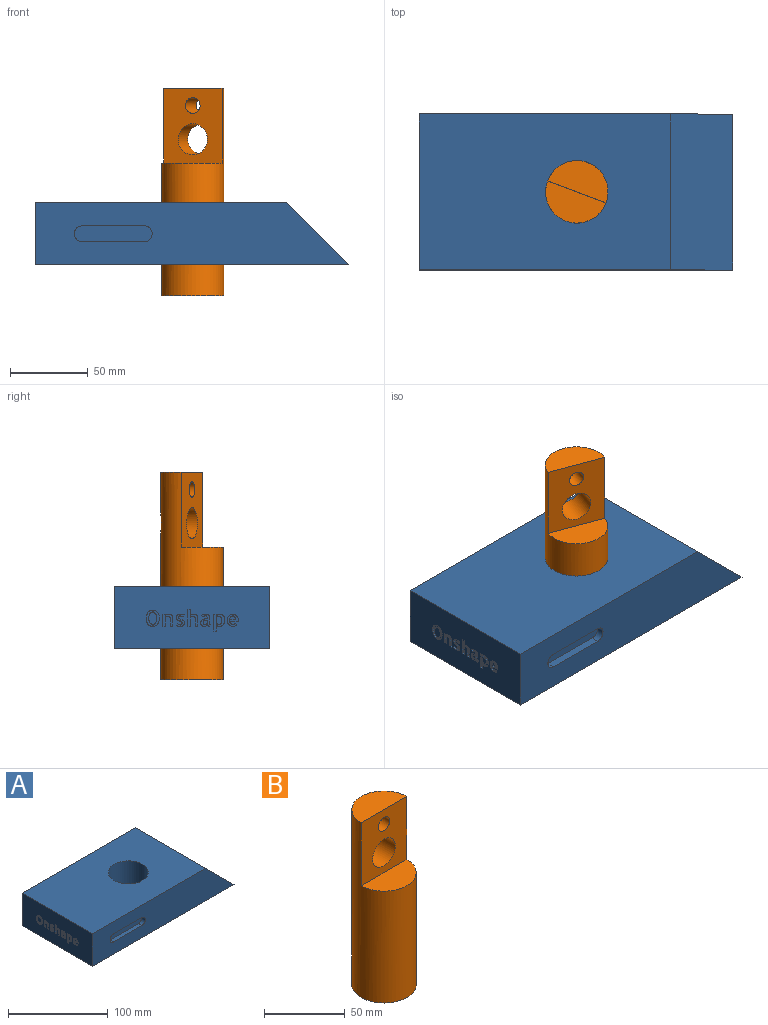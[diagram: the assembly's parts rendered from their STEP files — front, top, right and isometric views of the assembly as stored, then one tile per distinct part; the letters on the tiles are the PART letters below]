
ASSEMBLY  parts=2 mates=1
PART A: 284 faces, bbox 201x100x40 mm
  f0: plane 201x40mm, normal (0,1,0), area 7240mm2, adj f3,f4,f5,f252
  f1: plane 201x40mm, normal (0,-1,0), area 6761.5mm2, adj f3,f4,f5,f252,f269,f270,f271,f272
  f2: cylinder r=20mm len=40mm, axis (0,0,-1), area 5026.5mm2, adj f4,f5
  f3: plane 100x40mm, normal (0.71,0,0.71), area 5656.9mm2, adj f0,f1,f4,f5
  f4: plane 161x100mm, normal (0,0,1), area 14843.4mm2, adj f0,f1,f2,f3,f252
  f5: plane 201x100mm, normal (0,0,-1), area 17037mm2, adj f0,f1,f2,f3,f252,f274,f275,f276
  f6: extruded ~2.17x1mm, area 2.2mm2, adj f7,f251,f252,f253
  f7: extruded ~2.16x1mm, area 2.2mm2, adj f6,f8,f252,f253
  f8: extruded ~1.59x1mm, area 1.8mm2, adj f7,f9,f252,f253
  f9: extruded ~1.25x1mm, area 1.6mm2, adj f8,f10,f252,f253
  f10: extruded ~1.57x1mm, area 1.6mm2, adj f9,f11,f252,f253
  f11: plane 1.37x1mm, normal (0,1,0), area 1.4mm2, adj f10,f12,f252,f253
  f12: extruded ~1x0.88mm, area 0.9mm2, adj f11,f13,f252,f253
  f13: extruded ~1x0.71mm, area 1mm2, adj f12,f14,f252,f253
  f14: extruded ~1.15x1mm, area 1.3mm2, adj f13,f15,f252,f253
  f15: extruded ~1.66x1mm, area 1.7mm2, adj f14,f16,f252,f253
  f16: extruded ~1.67x1mm, area 1.7mm2, adj f15,f17,f252,f253
  f17: extruded ~1.16x1mm, area 1.3mm2, adj f16,f18,f252,f253
  f18: extruded ~1x0.72mm, area 1mm2, adj f17,f19,f252,f253
  f19: extruded ~1x0.86mm, area 0.9mm2, adj f18,f20,f252,f253
  f20: plane 1.36x1mm, normal (0,1,0), area 1.4mm2, adj f19,f21,f252,f253
  f21: extruded ~1.57x1mm, area 1.6mm2, adj f20,f22,f252,f253
  f22: extruded ~1.26x1mm, area 1.6mm2, adj f21,f251,f252,f253
  f23: plane 1.36x1mm, normal (0,-1,0), area 1.4mm2, adj f24,f236,f252,f268
  f24: extruded ~1.56x1mm, area 1.6mm2, adj f23,f25,f252,f268
  f25: extruded ~1.25x1.01mm, area 1.6mm2, adj f24,f26,f252,f268
  f26: extruded ~1.59x1mm, area 1.8mm2, adj f25,f27,f252,f268
  f27: extruded ~2.16x1mm, area 2.2mm2, adj f26,f28,f252,f268
  f28: extruded ~2.17x1mm, area 2.2mm2, adj f27,f29,f252,f268
  f29: extruded ~1.6x1mm, area 1.8mm2, adj f28,f30,f252,f268
  f30: extruded ~1.24x1mm, area 1.6mm2, adj f29,f31,f252,f268
  f31: extruded ~1.57x1mm, area 1.6mm2, adj f30,f32,f252,f268
  f32: plane 1.36x1mm, normal (0,-1,0), area 1.4mm2, adj f31,f33,f252,f268
  f33: extruded ~1x0.88mm, area 0.9mm2, adj f32,f34,f252,f268
  f34: extruded ~1x0.71mm, area 1mm2, adj f33,f35,f252,f268
  f35: extruded ~1.15x1mm, area 1.3mm2, adj f34,f36,f252,f268
  f36: extruded ~1.67x1mm, area 1.7mm2, adj f35,f37,f252,f268
  f37: extruded ~1.67x1mm, area 1.7mm2, adj f36,f38,f252,f268
  f38: extruded ~1.15x1mm, area 1.3mm2, adj f37,f39,f252,f268
  f39: extruded ~1x0.72mm, area 1mm2, adj f38,f236,f252,f268
  f40: plane 1.48x1mm, normal (0,0,-1), area 1.5mm2, adj f41,f237,f252,f267
  f41: plane 1x0.78mm, normal (0,0.98,-0.22), area 0.8mm2, adj f40,f42,f252,f267
  f42: plane 6.96x1mm, normal (0,1,0), area 7mm2, adj f41,f43,f252,f267
  f43: plane 1.66x1mm, normal (0,0,1), area 1.7mm2, adj f42,f237,f252,f267
  f44: extruded ~1x0.85mm, area 1.1mm2, adj f45,f238,f252,f266
  f45: extruded ~1x0.54mm, area 0.7mm2, adj f44,f46,f252,f266
  f46: extruded ~1x0.64mm, area 0.7mm2, adj f45,f47,f252,f266
  f47: extruded ~1x0.68mm, area 0.7mm2, adj f46,f48,f252,f266
  f48: extruded ~1x0.67mm, area 0.7mm2, adj f47,f49,f252,f266
  f49: plane 4.35x1mm, normal (0,1,0), area 4.4mm2, adj f48,f50,f252,f266
  f50: plane 1.67x1mm, normal (0,0,1), area 1.7mm2, adj f49,f51,f252,f266
  f51: plane 4.21x1mm, normal (0,-1,0), area 4.2mm2, adj f50,f52,f252,f266
  f52: extruded ~1x0.89mm, area 0.9mm2, adj f51,f53,f252,f266
  f53: extruded ~1x0.76mm, area 0.8mm2, adj f52,f54,f252,f266
  f54: extruded ~1x0.52mm, area 0.7mm2, adj f53,f55,f252,f266
  f55: extruded ~1x0.73mm, area 0.8mm2, adj f54,f56,f252,f266
  f56: extruded ~1x0.52mm, area 0.5mm2, adj f55,f57,f252,f266
  f57: extruded ~1x0.63mm, area 0.7mm2, adj f56,f58,f252,f266
  f58: plane 1.06x1mm, normal (0,-1,0), area 1.1mm2, adj f57,f59,f252,f266
  f59: extruded ~1x0.8mm, area 0.9mm2, adj f58,f60,f252,f266
  f60: extruded ~1x0.84mm, area 0.9mm2, adj f59,f238,f252,f266
  f61: extruded ~1.13x1mm, area 1.2mm2, adj f62,f239,f252,f265
  f62: extruded ~1x0.94mm, area 1mm2, adj f61,f63,f252,f265
  f63: extruded ~1x0.71mm, area 0.9mm2, adj f62,f64,f252,f265
  f64: extruded ~1x0.78mm, area 0.9mm2, adj f63,f65,f252,f265
  f65: extruded ~1x0.9mm, area 0.9mm2, adj f64,f66,f252,f265
  f66: plane 1.37x1mm, normal (0,1,0), area 1.4mm2, adj f65,f67,f252,f265
  f67: extruded ~1x0.56mm, area 0.6mm2, adj f66,f68,f252,f265
  f68: extruded ~1x0.62mm, area 0.7mm2, adj f67,f69,f252,f265
  f69: extruded ~1x0.53mm, area 0.6mm2, adj f68,f70,f252,f265
  f70: extruded ~1x0.54mm, area 0.6mm2, adj f69,f71,f252,f265
  f71: plane 1.47x1mm, normal (0,1,0), area 1.5mm2, adj f70,f72,f252,f265
  f72: extruded ~1x0.47mm, area 0.5mm2, adj f71,f73,f252,f265
  f73: extruded ~1x0.47mm, area 0.5mm2, adj f72,f239,f252,f265
  f74: plane 1.14x1mm, normal (0,0.9,0.43), area 1.3mm2, adj f75,f240,f252,f264
  f75: extruded ~1x0.79mm, area 0.8mm2, adj f74,f76,f252,f264
  f76: extruded ~1x0.83mm, area 0.8mm2, adj f75,f77,f252,f264
  f77: plane 1.36x1mm, normal (0,-1,0), area 1.4mm2, adj f76,f78,f252,f264
  f78: extruded ~1.14x1mm, area 1.2mm2, adj f77,f240,f252,f264
  f79: plane 1.11x1mm, normal (0,-0.85,-0.53), area 1.3mm2, adj f80,f241,f252,f263
  f80: extruded ~1x0.65mm, area 0.7mm2, adj f79,f81,f252,f263
  f81: extruded ~1x0.95mm, area 1mm2, adj f80,f82,f252,f263
  f82: plane 1x0.07mm, normal (0,0,-1), area 0.1mm2, adj f81,f83,f252,f263
  f83: plane 1.28x1mm, normal (0,1,0), area 1.3mm2, adj f82,f84,f252,f263
  f84: extruded ~1x0.63mm, area 0.6mm2, adj f83,f85,f252,f263
  f85: extruded ~1x0.57mm, area 0.6mm2, adj f84,f86,f252,f263
  f86: extruded ~1x0.57mm, area 0.6mm2, adj f85,f241,f252,f263
  f87: plane 1.46x1mm, normal (0,-1,0), area 1.5mm2, adj f88,f242,f252,f262
  f88: extruded ~1x0.84mm, area 0.9mm2, adj f87,f89,f252,f262
  f89: extruded ~1x0.78mm, area 0.9mm2, adj f88,f90,f252,f262
  f90: extruded ~1x0.61mm, area 0.8mm2, adj f89,f91,f252,f262
  f91: extruded ~1x0.91mm, area 1mm2, adj f90,f92,f252,f262
  f92: extruded ~1x0.93mm, area 1mm2, adj f91,f93,f252,f262
  f93: extruded ~1x0.69mm, area 0.9mm2, adj f92,f94,f252,f262
  f94: extruded ~1x0.76mm, area 0.9mm2, adj f93,f95,f252,f262
  f95: extruded ~1x0.95mm, area 1mm2, adj f94,f96,f252,f262
  f96: plane 1.3x1mm, normal (0,-1,0), area 1.3mm2, adj f95,f97,f252,f262
  f97: extruded ~1x0.72mm, area 0.8mm2, adj f96,f98,f252,f262
  f98: extruded ~1x0.57mm, area 0.6mm2, adj f97,f99,f252,f262
  f99: extruded ~1x0.56mm, area 0.6mm2, adj f98,f242,f252,f262
  f100: plane 10.67x1mm, normal (0,-1,0), area 10.7mm2, adj f101,f243,f252,f261
  f101: plane 1.66x1mm, normal (0,0,-1), area 1.7mm2, adj f100,f102,f252,f261
  f102: plane 10.67x1mm, normal (0,1,0), area 10.7mm2, adj f101,f243,f252,f261
  f103: extruded ~1x0.85mm, area 1.1mm2, adj f104,f244,f252,f260
  f104: extruded ~1x0.54mm, area 0.7mm2, adj f103,f105,f252,f260
  f105: extruded ~1x0.64mm, area 0.7mm2, adj f104,f106,f252,f260
  f106: extruded ~1x0.68mm, area 0.7mm2, adj f105,f107,f252,f260
  f107: extruded ~1x0.67mm, area 0.7mm2, adj f106,f108,f252,f260
  f108: plane 4.35x1mm, normal (0,1,0), area 4.4mm2, adj f107,f109,f252,f260
  f109: plane 1.67x1mm, normal (0,0,1), area 1.7mm2, adj f108,f110,f252,f260
  f110: plane 4.21x1mm, normal (0,-1,0), area 4.2mm2, adj f109,f111,f252,f260
  f111: extruded ~1x0.89mm, area 0.9mm2, adj f110,f112,f252,f260
  f112: extruded ~1x0.76mm, area 0.8mm2, adj f111,f113,f252,f260
  f113: extruded ~1x0.52mm, area 0.7mm2, adj f112,f114,f252,f260
  f114: extruded ~1x0.73mm, area 0.8mm2, adj f113,f115,f252,f260
  f115: extruded ~1x0.52mm, area 0.5mm2, adj f114,f116,f252,f260
  f116: extruded ~1x0.63mm, area 0.7mm2, adj f115,f117,f252,f260
  f117: plane 1.06x1mm, normal (0,-1,0), area 1.1mm2, adj f116,f118,f252,f260
  f118: extruded ~1x0.8mm, area 0.9mm2, adj f117,f119,f252,f260
  f119: extruded ~1x0.84mm, area 0.9mm2, adj f118,f244,f252,f260
  f120: extruded ~1x0.72mm, area 0.7mm2, adj f121,f245,f252,f259
  f121: extruded ~1x0.92mm, area 1mm2, adj f120,f122,f252,f259
  f122: extruded ~1x0.73mm, area 0.8mm2, adj f121,f123,f252,f259
  f123: plane 1.11x1mm, normal (0,1,0), area 1.1mm2, adj f122,f124,f252,f259
  f124: extruded ~1x0.18mm, area 0.2mm2, adj f123,f125,f252,f259
  f125: extruded ~1x0.9mm, area 0.9mm2, adj f124,f126,f252,f259
  f126: extruded ~1x0.76mm, area 0.9mm2, adj f125,f127,f252,f259
  f127: extruded ~1x0.73mm, area 0.9mm2, adj f126,f128,f252,f259
  f128: extruded ~1.11x1mm, area 1.1mm2, adj f127,f129,f252,f259
  f129: extruded ~1.09x1mm, area 1.1mm2, adj f128,f130,f252,f259
  f130: extruded ~1x0.76mm, area 1mm2, adj f129,f131,f252,f259
  f131: extruded ~1x0.95mm, area 1.1mm2, adj f130,f132,f252,f259
  f132: extruded ~1.08x1mm, area 1.1mm2, adj f131,f133,f252,f259
  f133: plane 1x0.6mm, normal (0,0,-1), area 0.6mm2, adj f132,f134,f252,f259
  f134: plane 1x0.98mm, normal (0,1,0), area 1mm2, adj f133,f135,f252,f259
  f135: plane 1x0.3mm, normal (0,0,1), area 0.3mm2, adj f134,f136,f252,f259
  f136: extruded ~1x0.58mm, area 0.6mm2, adj f135,f137,f252,f259
  f137: extruded ~1x0.56mm, area 0.6mm2, adj f136,f245,f252,f259
  f138: plane 1.89x1mm, normal (0,1,0), area 1.9mm2, adj f139,f246,f252,f258
  f139: extruded ~1x0.32mm, area 0.3mm2, adj f138,f140,f252,f258
  f140: extruded ~1x0.43mm, area 0.4mm2, adj f139,f141,f252,f258
  f141: extruded ~1x0.4mm, area 0.4mm2, adj f140,f142,f252,f258
  f142: extruded ~1x0.24mm, area 0.3mm2, adj f141,f143,f252,f258
  f143: plane 1x0.92mm, normal (0,0.9,0.43), area 1mm2, adj f142,f144,f252,f258
  f144: extruded ~1x0.38mm, area 0.4mm2, adj f143,f145,f252,f258
  f145: extruded ~1x0.38mm, area 0.5mm2, adj f144,f146,f252,f258
  f146: extruded ~1x0.34mm, area 0.5mm2, adj f145,f147,f252,f258
  f147: extruded ~1x0.41mm, area 0.5mm2, adj f146,f148,f252,f258
  f148: extruded ~1x0.61mm, area 0.8mm2, adj f147,f149,f252,f258
  f149: extruded ~1x0.9mm, area 1mm2, adj f148,f150,f252,f258
  f150: plane 1.04x1mm, normal (0,-1,0), area 1mm2, adj f149,f151,f252,f258
  f151: extruded ~1x0.6mm, area 0.7mm2, adj f150,f152,f252,f258
  f152: extruded ~1x0.47mm, area 0.7mm2, adj f151,f153,f252,f258
  f153: plane 2.9x1mm, normal (0,-1,0), area 2.9mm2, adj f152,f154,f252,f258
  f154: extruded ~1.07x1mm, area 1.1mm2, adj f153,f155,f252,f258
  f155: extruded ~1x0.58mm, area 0.6mm2, adj f154,f156,f252,f258
  f156: extruded ~1x0.41mm, area 0.5mm2, adj f155,f157,f252,f258
  f157: extruded ~1x0.57mm, area 0.6mm2, adj f156,f158,f252,f258
  f158: extruded ~1x0.57mm, area 0.6mm2, adj f157,f159,f252,f258
  f159: extruded ~1x0.49mm, area 0.5mm2, adj f158,f160,f252,f258
  f160: extruded ~1x0.4mm, area 0.5mm2, adj f159,f161,f252,f258
  f161: extruded ~1x0.25mm, area 0.3mm2, adj f160,f162,f252,f258
  f162: plane 1x0.95mm, normal (0,-0.84,0.55), area 1.1mm2, adj f161,f163,f252,f258
  f163: extruded ~1x0.41mm, area 0.5mm2, adj f162,f164,f252,f258
  f164: extruded ~1x0.63mm, area 0.7mm2, adj f163,f165,f252,f258
  f165: extruded ~1x0.78mm, area 0.8mm2, adj f164,f166,f252,f258
  f166: extruded ~1x0.87mm, area 0.9mm2, adj f165,f167,f252,f258
  f167: extruded ~1x0.8mm, area 0.8mm2, adj f166,f168,f252,f258
  f168: extruded ~1x0.71mm, area 0.8mm2, adj f167,f169,f252,f258
  f169: extruded ~1x0.56mm, area 0.8mm2, adj f168,f170,f252,f258
  f170: extruded ~1x0.8mm, area 0.9mm2, adj f169,f171,f252,f258
  f171: extruded ~1x0.97mm, area 1mm2, adj f170,f246,f252,f258
  f172: plane 1.5x1mm, normal (0,0,-1), area 1.5mm2, adj f173,f247,f252,f257
  f173: plane 1x0.78mm, normal (0,0.98,-0.22), area 0.8mm2, adj f172,f174,f252,f257
  f174: plane 10.01x1mm, normal (0,1,0), area 10mm2, adj f173,f175,f252,f257
  f175: plane 1.67x1mm, normal (0,0,1), area 1.7mm2, adj f174,f247,f252,f257
  f176: extruded ~1.13x1mm, area 1.2mm2, adj f177,f248,f252,f256
  f177: extruded ~1.41x1mm, area 1.4mm2, adj f176,f178,f252,f256
  f178: extruded ~1.52x1mm, area 1.5mm2, adj f177,f179,f252,f256
  f179: extruded ~1.3x1mm, area 1.4mm2, adj f178,f180,f252,f256
  f180: extruded ~1x0.95mm, area 1.3mm2, adj f179,f181,f252,f256
  f181: extruded ~1.34x1mm, area 1.4mm2, adj f180,f182,f252,f256
  f182: extruded ~1x0.91mm, area 0.9mm2, adj f181,f183,f252,f256
  f183: extruded ~1x0.75mm, area 0.8mm2, adj f182,f184,f252,f256
  f184: plane 1.43x1mm, normal (0,-1,0), area 1.4mm2, adj f183,f185,f252,f256
  f185: extruded ~1.11x1mm, area 1.3mm2, adj f184,f186,f252,f256
  f186: extruded ~1x0.75mm, area 0.8mm2, adj f185,f187,f252,f256
  f187: extruded ~1x0.58mm, area 0.8mm2, adj f186,f188,f252,f256
  f188: extruded ~1x0.84mm, area 0.9mm2, adj f187,f189,f252,f256
  f189: extruded ~1.04x1mm, area 1mm2, adj f188,f190,f252,f256
  f190: extruded ~1.02x1mm, area 1mm2, adj f189,f191,f252,f256
  f191: extruded ~1x0.85mm, area 0.9mm2, adj f190,f192,f252,f256
  f192: extruded ~1x0.59mm, area 0.8mm2, adj f191,f193,f252,f256
  f193: extruded ~1x0.75mm, area 0.8mm2, adj f192,f194,f252,f256
  f194: extruded ~1x0.65mm, area 0.7mm2, adj f193,f195,f252,f256
  f195: extruded ~1x0.53mm, area 0.7mm2, adj f194,f196,f252,f256
  f196: plane 1.46x1mm, normal (0,-1,0), area 1.5mm2, adj f195,f197,f252,f256
  f197: extruded ~1x0.7mm, area 0.8mm2, adj f196,f198,f252,f256
  f198: extruded ~1x0.8mm, area 0.8mm2, adj f197,f199,f252,f256
  f199: extruded ~1x0.92mm, area 0.9mm2, adj f198,f200,f252,f256
  f200: extruded ~1x0.87mm, area 1mm2, adj f199,f248,f252,f256
  f201: plane 1.29x1mm, normal (0,-1,0), area 1.3mm2, adj f202,f249,f252,f255
  f202: extruded ~1.34x1mm, area 1.4mm2, adj f201,f203,f252,f255
  f203: extruded ~1.02x1mm, area 1.3mm2, adj f202,f204,f252,f255
  f204: extruded ~1.19x1mm, area 1.4mm2, adj f203,f205,f252,f255
  f205: extruded ~1.4x1mm, area 1.4mm2, adj f204,f206,f252,f255
  f206: extruded ~1x0.66mm, area 0.7mm2, adj f205,f207,f252,f255
  f207: plane 4.71x1mm, normal (0,0,1), area 4.7mm2, adj f206,f208,f252,f255
  f208: plane 1.21x1mm, normal (0,-1,0), area 1.2mm2, adj f207,f209,f252,f255
  f209: plane 3.17x1mm, normal (0,0,-1), area 3.2mm2, adj f208,f210,f252,f255
  f210: extruded ~1x0.69mm, area 0.7mm2, adj f209,f211,f252,f255
  f211: extruded ~1x0.61mm, area 0.7mm2, adj f210,f212,f252,f255
  f212: extruded ~1x0.53mm, area 0.7mm2, adj f211,f249,f252,f255
  f213: extruded ~1x0.98mm, area 1mm2, adj f214,f250,f252,f254
  f214: extruded ~1x0.38mm, area 0.4mm2, adj f213,f215,f252,f254
  f215: extruded ~1x0.48mm, area 0.5mm2, adj f214,f216,f252,f254
  f216: extruded ~1x0.51mm, area 0.6mm2, adj f215,f217,f252,f254
  f217: extruded ~1x0.45mm, area 0.6mm2, adj f216,f218,f252,f254
  f218: plane 1x0.92mm, normal (0,0.84,-0.55), area 1.1mm2, adj f217,f219,f252,f254
  f219: extruded ~1.06x1mm, area 1.4mm2, adj f218,f220,f252,f254
  f220: extruded ~1.54x1mm, area 1.6mm2, adj f219,f221,f252,f254
  f221: extruded ~1.41x1mm, area 1.5mm2, adj f220,f222,f252,f254
  f222: extruded ~1.13x1mm, area 1.4mm2, adj f221,f223,f252,f254
  f223: extruded ~1.25x1mm, area 1.5mm2, adj f222,f224,f252,f254
  f224: extruded ~1.54x1mm, area 1.6mm2, adj f223,f225,f252,f254
  f225: extruded ~1.48x1mm, area 1.5mm2, adj f224,f226,f252,f254
  f226: extruded ~1.23x1mm, area 1.4mm2, adj f225,f227,f252,f254
  f227: extruded ~1.02x1mm, area 1.3mm2, adj f226,f228,f252,f254
  f228: extruded ~1.26x1mm, area 1.3mm2, adj f227,f229,f252,f254
  f229: plane 1.32x1mm, normal (0,1,0), area 1.3mm2, adj f228,f230,f252,f254
  f230: extruded ~1x0.84mm, area 0.9mm2, adj f229,f231,f252,f254
  f231: extruded ~1x0.72mm, area 0.9mm2, adj f230,f232,f252,f254
  f232: extruded ~1x0.83mm, area 0.9mm2, adj f231,f233,f252,f254
  f233: extruded ~1x0.73mm, area 0.7mm2, adj f232,f234,f252,f254
  f234: extruded ~1x1mm, area 1mm2, adj f233,f235,f252,f254
  f235: extruded ~1x0.8mm, area 0.9mm2, adj f234,f250,f252,f254
  f236: extruded ~1x0.86mm, area 0.9mm2, adj f23,f39,f252,f268
  f237: plane 7.74x1mm, normal (0,-1,0), area 7.7mm2, adj f40,f43,f252,f267
  f238: extruded ~1.04x1mm, area 1.1mm2, adj f44,f60,f252,f266
  f239: extruded ~1.09x1mm, area 1.4mm2, adj f61,f73,f252,f265
  f240: extruded ~1.02x1mm, area 1.1mm2, adj f74,f78,f252,f264
  f241: extruded ~1x0.6mm, area 0.7mm2, adj f79,f86,f252,f263
  f242: extruded ~1x0.69mm, area 0.8mm2, adj f87,f99,f252,f262
  f243: plane 1.66x1mm, normal (0,0,1), area 1.7mm2, adj f100,f102,f252,f261
  f244: extruded ~1.04x1mm, area 1.1mm2, adj f103,f119,f252,f260
  f245: extruded ~1x0.43mm, area 0.6mm2, adj f120,f137,f252,f259
  f246: extruded ~1x0.97mm, area 1mm2, adj f138,f171,f252,f258
  f247: plane 10.79x1mm, normal (0,-1,0), area 10.8mm2, adj f172,f175,f252,f257
  f248: extruded ~1x0.76mm, area 1.1mm2, adj f176,f200,f252,f256
  f249: extruded ~1x0.67mm, area 0.7mm2, adj f201,f212,f252,f255
  f250: extruded ~1x0.68mm, area 0.9mm2, adj f213,f235,f252,f254
  f251: extruded ~1.6x1mm, area 1.8mm2, adj f6,f22,f252,f253
  f252: plane 100x40mm, normal (-1,0,0), area 3792.3mm2, adj f0,f1,f4,f5,f6,f7,f8,f9
  f253: plane 10.34x3.94mm, normal (-1,0,0), area 18.8mm2, adj f6,f7,f8,f9,f10,f11,f12,f13
  f254: plane 7.88x6.15mm, normal (-1,0,0), area 16.5mm2, adj f213,f214,f215,f216,f217,f218,f219,f220
  f255: plane 4.75x4.5mm, normal (-1,0,0), area 11.1mm2, adj f201,f202,f203,f204,f205,f206,f207,f208
  f256: plane 7.88x4.7mm, normal (-1,0,0), area 18.6mm2, adj f176,f177,f178,f179,f180,f181,f182,f183
  f257: plane 10.79x1.67mm, normal (-1,0,0), area 18mm2, adj f172,f173,f174,f175,f247
  f258: plane 7.81x5.71mm, normal (-1,0,0), area 16.7mm2, adj f138,f139,f140,f141,f142,f143,f144,f145
  f259: plane 4.79x3.6mm, normal (-1,0,0), area 8.8mm2, adj f120,f121,f122,f123,f124,f125,f126,f127
  f260: plane 7.83x4.19mm, normal (-1,0,0), area 15mm2, adj f103,f104,f105,f106,f107,f108,f109,f110
  f261: plane 10.67x1.66mm, normal (-1,0,0), area 17.7mm2, adj f100,f101,f102,f243
  f262: plane 4.53x2.42mm, normal (-1,0,0), area 7mm2, adj f87,f88,f89,f90,f91,f92,f93,f94
  f263: plane 2.37x1.8mm, normal (-1,0,0), area 2.8mm2, adj f79,f80,f81,f82,f83,f84,f85,f86
  f264: plane 2.16x1.77mm, normal (-1,0,0), area 2.6mm2, adj f74,f75,f76,f77,f78,f240
  f265: plane 4.63x2.4mm, normal (-1,0,0), area 7.4mm2, adj f61,f62,f63,f64,f65,f66,f67,f68
  f266: plane 7.83x4.19mm, normal (-1,0,0), area 15mm2, adj f44,f45,f46,f47,f48,f49,f50,f51
  f267: plane 7.74x1.66mm, normal (-1,0,0), area 12.8mm2, adj f40,f41,f42,f43,f237
  f268: plane 10.34x3.94mm, normal (-1,0,0), area 18.8mm2, adj f23,f24,f25,f26,f27,f28,f29,f30
  f269: plane 40x5mm, normal (0,0,-1), area 200mm2, adj f1,f270,f272,f273
  f270: cylinder r=5mm len=10mm, axis (0,-1,0), area 78.5mm2, adj f1,f269,f271,f273
  f271: plane 40x5mm, normal (0,0,1), area 200mm2, adj f1,f270,f272,f273
  f272: cylinder r=5mm len=10mm, axis (0,-1,0), area 78.5mm2, adj f1,f269,f271,f273
  f273: plane 50x10mm, normal (0,-1,0), area 478.5mm2, adj f269,f270,f271,f272
  f274: cylinder r=21.65mm len=34.77mm, axis (0,0,-1), area 404.3mm2, adj f5,f275,f277,f278
  f275: cylinder r=5mm len=10mm, axis (0,0,-1), area 157.1mm2, adj f5,f274,f276,f278
  f276: cylinder r=31.65mm len=50.83mm, axis (0,0,-1), area 591.1mm2, adj f5,f275,f277,f278
  f277: cylinder r=5mm len=10mm, axis (0,0,-1), area 157.1mm2, adj f5,f274,f276,f278
  f278: plane 52.8x21.85mm, normal (0,0,-1), area 576.3mm2, adj f274,f275,f276,f277
  f279: extruded ~74.48x44.2mm, area 1113.5mm2, adj f5,f280,f282,f283
  f280: cylinder r=5mm len=10mm, axis (0,0,-1), area 157.1mm2, adj f5,f279,f281,f283
  f281: extruded ~74.92x49.03mm, area 1166.7mm2, adj f5,f280,f282,f283
  f282: cylinder r=5mm len=10mm, axis (0,0,-1), area 157.1mm2, adj f5,f279,f281,f283
  f283: plane 84.71x56.61mm, normal (0,0,-1), area 1220.9mm2, adj f279,f280,f281,f282
PART B: 7 faces, bbox 40x40x132.9 mm
  f0: cylinder r=20mm len=132.86mm, axis (0,0,-1), area 13283.7mm2, adj f1,f2,f3,f4,f5,f6
  f1: plane 40x40mm, normal (0,0,-1), area 1256.6mm2, adj f0
  f2: plane 47.86x40mm, normal (0,-1,0), area 1521.5mm2, adj f0,f3,f4,f5,f6
  f3: plane 40x20mm, normal (0,0,1), area 628.3mm2, adj f0,f2
  f4: plane 40x20mm, normal (0,0,1), area 628.3mm2, adj f0,f2
  f5: cylinder r=10mm len=20mm, axis (0,-1,0), area 1174mm2, adj f0,f2
  f6: cylinder r=5mm len=20mm, axis (0,-1,0), area 618.4mm2, adj f0,f2
PLACE A at identity fixed
PLACE B rot(axis=(0,0,-1),20.5deg) t=(0,0,-19.68)mm
MATE cylindrical B.f0 <-> A.f2  axis (0,0,-1) through (0,0,-19.68)mm
